# Revit family: PD11-FP types Avec hôte
name_source: partatom
category: Dispositifs d'éclairage
units: mm (PartAtom-declared; Revit-internal decimal feet)

## family parameters
Conserver l'orientation des annotations = Oui
Cote de connecteur circulaire = Utiliser le diamètre
Couper avec des vides une fois chargée = Non
Hôte = Face
Partagée = Non
Point de calcul de pièce = Non
Type d'élément = Normal

## types (12) — shared parameters
Classe = II
Code d'assemblage = D5010200
Fabricant = B.E.G.
Hauteur de montage max = 300 cm
Image du type = 360°.jpg
Marque = LUXOMAT
Mode de pose = Faux Plafond
Température ambiante = -25°C à +50°C
URL = http://www.luxomat.com
zero-valued in all types: Elévation par défaut

## per-type parameters (varying)
| type | Alimentation | Charge Cos ɸ =0.5 | Charge Cos ɸ =1 | Charge LED | Commentaires du type | Consommation | IP | Modèle | Relais | Référence | Type de Sortie |
| 01- PD11-FP Générique | 110-240 V AC |  |  |  | EXTRA PLAT.DET.PRES.360°/Ø9M FAUX PLAFOND |  | 20 | PD11-FP |  |  |  |
| 02- PD11-M-1C-FP réf 92583 | 110-240 V AC | 1150 VA | 2300 W | 300 W | EXTRA PLAT.DET.PRES.MAITRE.1 CONTACT.360°/Ø9M FAUX PLAFOND | 0,30 W | 20 | PD11-M-1C-FP | 10 A | 92583 | TOR |
| 10- PD11-KNX-DX-FP réf 93392 | 24 V DC par Bus KNX | 0 | 0 | 0 | EXTRA PLAT.DET.PRES.KNX.VERSION DELUXE.360°/Ø9M FAUX PLAFOND | 12 mA | 54 | PD11-KNX-DX-FP | 0 | 93392 | KNX - 1 sortie Eclairage TOR ou GRADATION / 3 sorties Présence / Capteur de température |
| 04- PD11-S-FP réf 92593 | 110-240 V AC | 0 | 0 | 0 | EXTRA PLAT.DET.PRES.ESCLAVE.360°/Ø9M FAUX PLAFOND | 0,25 W | 20 | PD11-S-FP | 0 | 92593 | Esclave |
| 06- PD11-DALISYS-FP réf 92731 | 10-22 V DC par Bus DALI | 0 | 0 | 0 | EXTRA PLAT.MULTI.CAPTEUR.PRES.DALISYS.360°/Ø9M FAUX PLAFOND | 7 mA | 20 | PD11-DALISYS-FP | 0 | 92731 | DALI Adressable |
| 05- PD11-DALILINK-FP réf 93068 | 16 V DC par Bus DALI | 0 | 0 | 0 | EXTRA PLAT.MULTI.CAPTEUR.PRES.DALILINK.360°/Ø9M FAUX PLAFOND | 4 mA | 20 | PD11-DALILINK-FP | 0 | 93068 | DALILINK |
| 09- PD11-KNX-ST-FP réf 93802 | 24 V DC par Bus KNX | 0 | 0 | 0 | EXTRA PLAT.DET.PRES.KNX.VERSION STANDARD.360°/Ø9M FAUX PLAFOND | 12 mA | 54 | PD11-KNX-ST-FP | 0 | 93802 | KNX - 1 sortie Eclairage TOR ou GRADATION / 3 sorties Présence |
| 08- PD11-KNX-BA-FP réf 93803 | 24 V DC par Bus KNX | 0 | 0 | 0 | EXTRA PLAT.DET.PRES.KNX.VERSION BASIQUE.360°/Ø9M FAUX PLAFOND | 12 mA | 54 | PD11-KNX-BA-FP | 0 | 93803 | KNX - 1 sortie Eclairage TOR |
| 07- PD11-BMS-DALI-2-FP réf 93542 | 10-22 V DC par Bus DALI | 0 | 0 | 0 | EXTRA PLAT.MULTI.CAPTEUR.PRES.BMS.DALI 2.360°/Ø9M FAUX PLAFOND | 7 mA | 20 | PD11-BMS-DALI-2-FP | 0 | 93542 | DALI 2 Adressable |
| 11- PD11-KNXs-ST-FP réf 93522 | 24 V DC par Bus KNX | 0 | 0 | 0 | EXTRA PLAT.DET.PRES.KNX Sécure.VERSION STANDARD.360°/Ø9M FAUX PLAFOND | 12 mA | 54 | PD11-KNXs-ST-FP | 0 | 93522 | KNX Sécure - 1 sortie Eclairage TOR ou GRADATION / 3 sorties Présence |
| 12- PD11-KNXs-DX-FP réf 93523 | 24 V DC par Bus KNX | 0 | 0 | 0 | EXTRA PLAT.DET.PRES.KNX Sécure.VERSION DELUXE.360°/Ø9M FAUX PLAFOND | 12 mA | 54 | PD11-KNXs-DX-FP | 0 | 93523 | KNX Sécure - 1 sortie Eclairage TOR ou GRADATION / 3 sorties Présence / HCL |
| 03- PD11-M-DACO-FP réf 93459 | 110-240 V AC | 0 | 0 | 0 | EXTRA PLAT.DET.PRES.MAITRE.DALI 2.360°/Ø9M FAUX PLAFOND | 2 W | 20 | PD11-M-DACO-FP | 0 | 93459 | DALI 2  (40 drivers maxi) |

## geometry (parser evidence)
native form markers: Extrusion x2
no freeform markers — native parametric forms only
